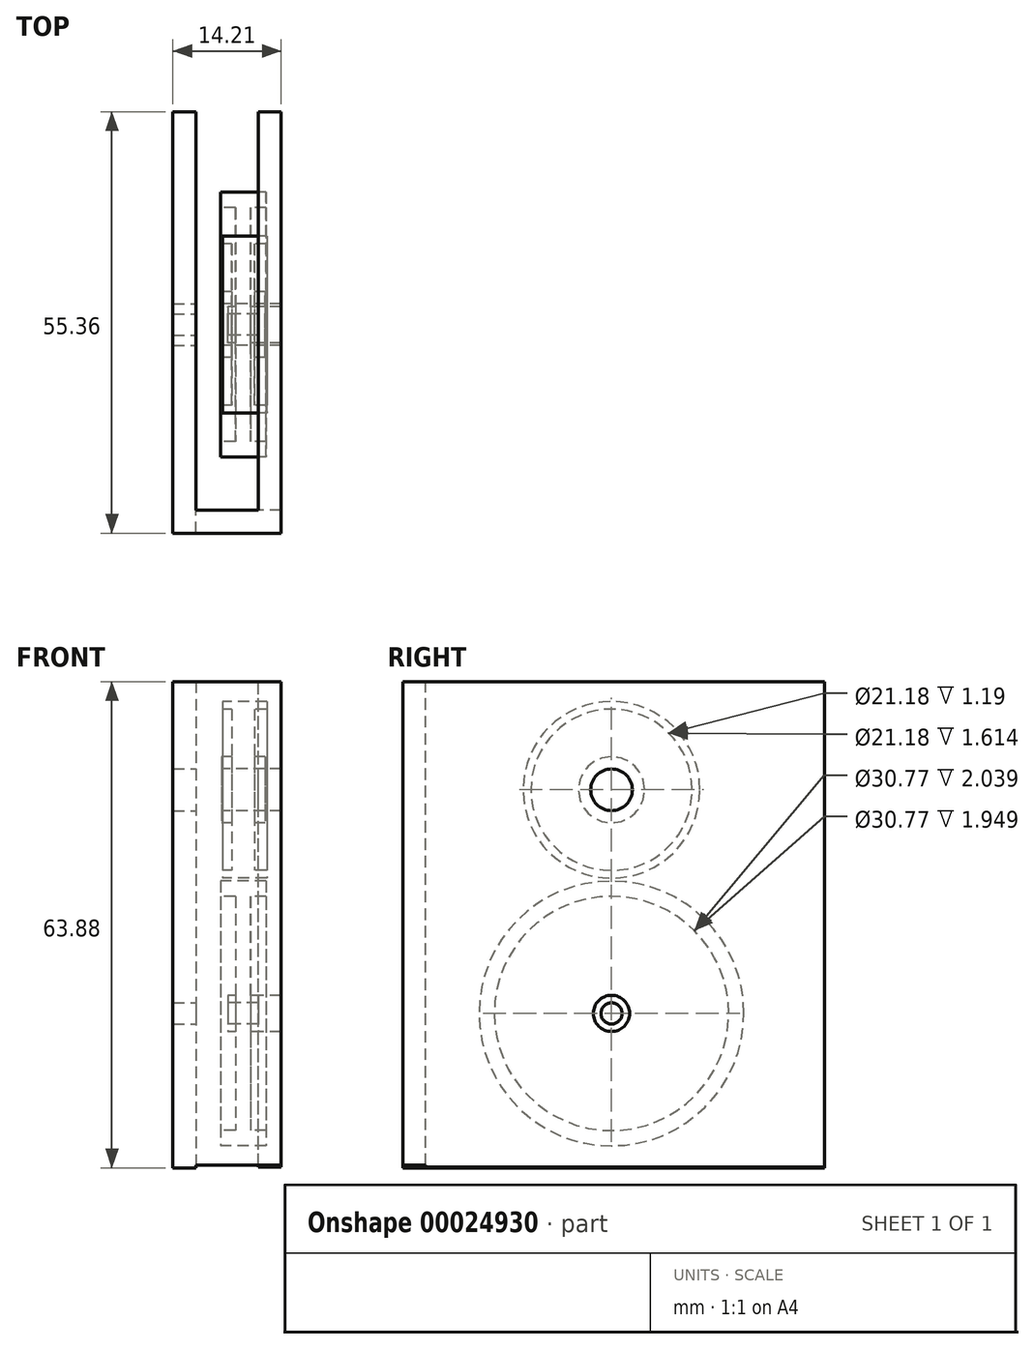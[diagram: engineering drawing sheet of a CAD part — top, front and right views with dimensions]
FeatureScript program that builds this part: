
annotation { "Feature Type Name" : "Feature", "Feature Type Description" : "" }
export const myFeature = defineFeature(function(context is Context, id is Id, definition is map)
    precondition{}
    {
        {
            var Q0;
            Q0=qCreatedBy(makeId("Front.planeOp"),FACE);
            var sketch = newSketch(context, id + "F0", { "sketchPlane" : qUnion([Q0])});
            skLineSegment(sketch, "E0", {"start": v(-15.34, 17.37) * mm, "end": v(-11.35, 17.37) * mm});
            skLineSegment(sketch, "E1", {"start": v(-15.34, 17.37) * mm, "end": v(-15.34, 17.5) * mm});
            skLineSegment(sketch, "E2", {"start": v(-11.35, 17.37) * mm, "end": v(-11.35, 18.36) * mm});
            skLineSegment(sketch, "E3", {"start": v(-15.34, 17.37) * mm, "end": v(-15.34, 18.36) * mm});
            skLineSegment(sketch, "E4", {"start": v(-15.34, 18.36) * mm, "end": v(-11.35, 18.36) * mm});
            skPoint(sketch, "E5", {"position": v(-13.35, 18.36) * mm});
            skLineSegment(sketch, "E6", {"start": v(-13.35, 18.36) * mm, "end": v(-15.34, 18.36) * mm});
            skLineSegment(sketch, "E7", {"start": v(-13.35, 18.36) * mm, "end": v(-11.35, 18.36) * mm});
            skPoint(sketch, "E8", {"position": v(-14.34, 18.36) * mm});
            skPoint(sketch, "E9", {"position": v(-12.35, 18.36) * mm});
            skLineSegment(sketch, "E10", {"start": v(-14.34, 18.36) * mm, "end": v(-14.34, 31.37) * mm});
            skLineSegment(sketch, "E11", {"start": v(-14.34, 31.37) * mm, "end": v(-12.34, 31.37) * mm});
            skLineSegment(sketch, "E12", {"start": v(-12.35, 18.36) * mm, "end": v(-12.34, 31.37) * mm});
            skLineSegment(sketch, "E13", {"start": v(-10.3, 31.37) * mm, "end": v(-16.3, 31.37) * mm});
            skLineSegment(sketch, "E14.bottom", {"start": v(-16.3, 31.37) * mm, "end": v(-10.3, 31.37) * mm});
            skLineSegment(sketch, "E14.top", {"start": v(-16.3, 33.38) * mm, "end": v(-10.3, 33.38) * mm});
            skLineSegment(sketch, "E14.left", {"start": v(-16.3, 31.37) * mm, "end": v(-16.3, 33.38) * mm});
            skLineSegment(sketch, "E14.right", {"start": v(-10.3, 31.37) * mm, "end": v(-10.3, 33.38) * mm});
            skLineSegment(sketch, "E15", {"start": v(-25, 15.98) * mm, "end": v(2.64, 15.98) * mm, "construction": true});
            skSolve(sketch);
        }
        {
            var Q0;
            {var subQ8=sQuery(id+"F0.wireOp",EDGE,"E0");Q0=makeQuery(id+"F0.imprint","IMPRINT",FACE,{"disambiguationData":[TD([[makeQuery(id+"F0.imprint","IMPRINT",EDGE,{"derivedFrom":subQ8}),1.0]])]});}
            var Q1;
            {var subQ2=sQuery(id+"F0.wireOp",EDGE,"E10");Q1=makeQuery(id+"F0.imprint","IMPRINT",FACE,{"disambiguationData":[TD([[makeQuery(id+"F0.imprint","IMPRINT",EDGE,{"derivedFrom":subQ2}),-1.0]])]});}
            var Q2;
            Q2=makeQuery(id+"F0.imprint","IMPRINT",FACE,{"disambiguationData":[TD([[makeQuery(id+"F0.imprint","IMPRINT",EDGE,{"derivedFrom":sQuery(id+"F0.wireOp",EDGE,"E14.top")}),-1.0]])]});
            var Q3;
            Q3=sQuery(id+"F0.wireOp",EDGE,"E15");
            revolve(context, id + "F1", {"entities" : qUnion([Q0, Q1, Q2]), "axis" : qUnion([Q3]), "revolveType" : RevolveType.FULL});
        }
        {
            var Q0;
            Q0=qCreatedBy(makeId("Front.planeOp"),FACE);
            var sketch = newSketch(context, id + "F2", { "sketchPlane" : qUnion([Q0])});
            skLineSegment(sketch, "E16.top", {"start": v(-14.83, 41.03) * mm, "end": v(-11.84, 41.03) * mm});
            skLineSegment(sketch, "E17.top", {"start": v(-16.2, 42.63) * mm, "end": v(-10.45, 42.63) * mm});
            skLineSegment(sketch, "E16.right", {"start": v(-11.84, 34.78) * mm, "end": v(-11.84, 41.03) * mm});
            skLineSegment(sketch, "E16.left", {"start": v(-14.83, 34.78) * mm, "end": v(-14.83, 41.03) * mm});
            skLineSegment(sketch, "E16.bottom", {"start": v(-14.83, 34.78) * mm, "end": v(-11.84, 34.78) * mm});
            skLineSegment(sketch, "E18.bottom", {"start": v(-16.02, 33.76) * mm, "end": v(-10.23, 33.76) * mm});
            skLineSegment(sketch, "E17.bottom", {"start": v(-16.2, 41.03) * mm, "end": v(-10.45, 41.03) * mm});
            skLineSegment(sketch, "E18.top", {"start": v(-16.02, 34.78) * mm, "end": v(-10.23, 34.78) * mm});
            skLineSegment(sketch, "E17.left", {"start": v(-16.2, 41.03) * mm, "end": v(-16.2, 42.63) * mm});
            skLineSegment(sketch, "E17.right", {"start": v(-10.45, 41.03) * mm, "end": v(-10.45, 42.63) * mm});
            skLineSegment(sketch, "E18.left", {"start": v(-16.02, 33.76) * mm, "end": v(-16.02, 34.78) * mm});
            skLineSegment(sketch, "E18.right", {"start": v(-10.23, 33.76) * mm, "end": v(-10.23, 34.78) * mm});
            skLineSegment(sketch, "E19", {"start": v(-22.7, 45.36) * mm, "end": v(-0.35, 45.36) * mm, "construction": true});
            skSolve(sketch);
        }
        {
            var Q0;
            Q0 = qSketchRegion(id + "F2", true);
            var Q1;
            Q1=sQuery(id+"F2.wireOp",EDGE,"E19");
            revolve(context, id + "F3", {"entities" : qUnion([Q0]), "axis" : qUnion([Q1]), "revolveType" : RevolveType.FULL});
        }
        {
            var Q0;
            Q0=makeQuery(id+"F1.opRevolve","SWEPT_FACE",FACE,{"disambiguationData":[OSD([sQuery(id+"F0.wireOp",EDGE,"E2")])]});
            var sketch = newSketch(context, id + "F4", { "sketchPlane" : qUnion([Q0])});
            skLineSegment(sketch, "E20.bottom", {"start": v(27.97, -4.2) * mm, "end": v(-24.4, -4.2) * mm});
            skLineSegment(sketch, "E20.top", {"start": v(27.97, 59.58) * mm, "end": v(-24.4, 59.58) * mm});
            skLineSegment(sketch, "E20.left", {"start": v(27.97, -4.2) * mm, "end": v(27.97, 59.58) * mm});
            skLineSegment(sketch, "E20.right", {"start": v(-24.4, -4.2) * mm, "end": v(-24.4, 59.58) * mm});
            skPoint(sketch, "E21", {"position": v(0, 45.36) * mm});
            skCircle(sketch, "E22", {"center": v(0, 45.36) * mm, "radius": 2.74 * mm});
            skSolve(sketch);
        }
        {
            var Q0;
            Q0=makeQuery(id+"F4.imprint","IMPRINT",FACE,{"disambiguationData":[TD([[makeQuery(id+"F4.imprint","IMPRINT",EDGE,{"derivedFrom":sQuery(id+"F4.wireOp",EDGE,"E20.bottom")}),-1.0]])]});
            extrude(context, id + "F5", {"entities" : qUnion([Q0]), "depth" : 3 * mm});
        }
        {
            var Q0;
            Q0=makeQuery(id+"F5.opExtrude","SWEPT_FACE",FACE,{"disambiguationData":[OSD([sQuery(id+"F4.wireOp",EDGE,"E20.right")])]});
            var sketch = newSketch(context, id + "F6", { "sketchPlane" : qUnion([Q0])});
            skLineSegment(sketch, "E23.bottom", {"start": v(-8.35, 59.58) * mm, "end": v(-19.56, 59.58) * mm});
            skLineSegment(sketch, "E23.top", {"start": v(-8.35, -3.93) * mm, "end": v(-19.56, -3.93) * mm});
            skLineSegment(sketch, "E23.left", {"start": v(-8.35, 59.58) * mm, "end": v(-8.35, -3.93) * mm});
            skLineSegment(sketch, "E23.right", {"start": v(-19.56, 59.58) * mm, "end": v(-19.56, -3.93) * mm});
            skSolve(sketch);
        }
        {
            var Q0;
            Q0 = qSketchRegion(id + "F6", true);
            extrude(context, id + "F7", {"entities" : qUnion([Q0]), "operationType" : NewBodyOperationType.ADD, "depth" : 3 * mm});
        }
        {
            var Q0;
            Q0=makeQuery(id+"F7.opExtrude","SWEPT_FACE",FACE,{"disambiguationData":[OSD([sQuery(id+"F6.wireOp",EDGE,"E23.right")])]});
            var sketch = newSketch(context, id + "F8", { "sketchPlane" : qUnion([Q0])});
            skLineSegment(sketch, "E24.bottom", {"start": v(27.4, 59.58) * mm, "end": v(-27.97, 59.58) * mm});
            skLineSegment(sketch, "E24.top", {"start": v(27.4, -4.3) * mm, "end": v(-27.97, -4.3) * mm});
            skLineSegment(sketch, "E24.left", {"start": v(27.4, 59.58) * mm, "end": v(27.4, -4.3) * mm});
            skLineSegment(sketch, "E24.right", {"start": v(-27.97, 59.58) * mm, "end": v(-27.97, -4.3) * mm});
            skPoint(sketch, "E25", {"position": v(0, 45.36) * mm});
            skPoint(sketch, "E26", {"position": v(0, 15.98) * mm});
            skCircle(sketch, "E27", {"center": v(0, 45.36) * mm, "radius": 2.74 * mm});
            skCircle(sketch, "E28", {"center": v(0, 15.98) * mm, "radius": 1.39 * mm});
            skSolve(sketch);
        }
        {
            var Q0;
            Q0 = qSketchRegion(id + "F8", true);
            extrude(context, id + "F9", {"entities" : qUnion([Q0]), "operationType" : NewBodyOperationType.ADD, "depth" : 3 * mm});
        }
    });
